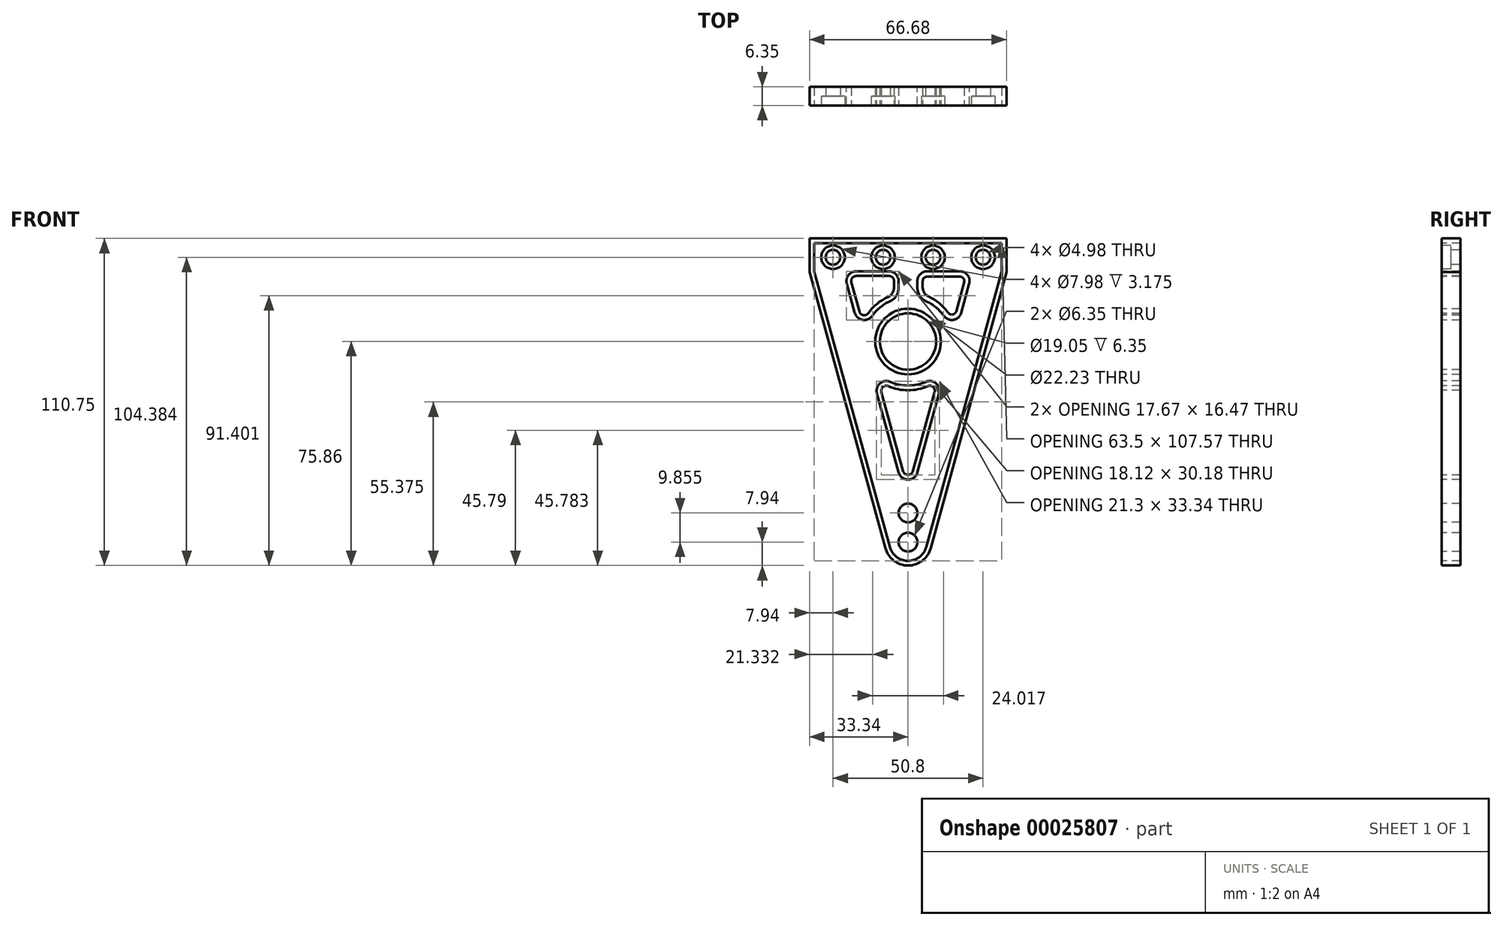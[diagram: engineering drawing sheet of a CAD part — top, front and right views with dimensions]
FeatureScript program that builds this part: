
annotation { "Feature Type Name" : "Feature", "Feature Type Description" : "" }
export const myFeature = defineFeature(function(context is Context, id is Id, definition is map)
    precondition{}
    {
        {
            var Q0;
            Q0=qCreatedBy(makeId("Front.planeOp"),FACE);
            var sketch = newSketch(context, id + "F0", { "sketchPlane" : qUnion([Q0])});
            skCircle(sketch, "E0", {"center": v(0, 0) * mm, "radius": 11.11 * mm});
            skLineSegment(sketch, "E1", {"start": v(0, 0) * mm, "end": v(0, 38.71) * mm, "construction": true});
            skLineSegment(sketch, "E2", {"start": v(0, 0) * mm, "end": v(56.24, 0) * mm, "construction": true});
            skLineSegment(sketch, "E3", {"start": v(0, 33.3) * mm, "end": v(31.75, 33.3) * mm});
            skLineSegment(sketch, "E4", {"start": v(31.75, 33.3) * mm, "end": v(31.75, 23.77) * mm});
            skLineSegment(sketch, "E5", {"start": v(31.75, 23.77) * mm, "end": v(6.12, -69.6) * mm});
            skLineSegment(sketch, "E6", {"start": v(-6.12, -69.6) * mm, "end": v(-31.75, 23.77) * mm});
            skLineSegment(sketch, "E7", {"start": v(-31.75, 23.77) * mm, "end": v(-31.75, 33.3) * mm});
            skLineSegment(sketch, "E8", {"start": v(-31.75, 33.3) * mm, "end": v(0, 33.3) * mm});
            skArc(sketch, "E9", {"start": v(-6.12, -69.6) * mm, "mid": v(0, -74.27) * mm, "end": v(6.12, -69.6) * mm});
            skPoint(sketch, "E10", {"position": v(0, -74.27) * mm});
            skLineSegment(sketch, "E11", {"start": v(-49.73, 28.52) * mm, "end": v(49.74, 28.52) * mm, "construction": true});
            skPoint(sketch, "E12", {"position": v(-25.4, 28.52) * mm});
            skPoint(sketch, "E13", {"position": v(-8.46, 28.52) * mm});
            skPoint(sketch, "E14", {"position": v(8.46, 28.52) * mm});
            skPoint(sketch, "E15", {"position": v(25.4, 28.52) * mm});
            skSolve(sketch);
        }
        {
            var Q0;
            Q0=makeQuery(id+"F0.imprint","IMPRINT",FACE,{"disambiguationData":[TD([[makeQuery(id+"F0.imprint","IMPRINT",EDGE,{"derivedFrom":sQuery(id+"F0.wireOp",EDGE,"E0")}),-1.0]])]});
            extrude(context, id + "F1", {"entities" : qUnion([Q0]), "depth" : 6.35 * mm});
        }
        {
            var Q0;
            Q0=makeQuery(id+"F1.opExtrude","CAP_FACE",FACE,{"disambiguationData":[OSD([sQuery(id+"F0.wireOp",EDGE,"E0"),sQuery(id+"F0.wireOp",EDGE,"E3"),sQuery(id+"F0.wireOp",EDGE,"E4"),sQuery(id+"F0.wireOp",EDGE,"E5"),sQuery(id+"F0.wireOp",EDGE,"E6"),sQuery(id+"F0.wireOp",EDGE,"E7"),sQuery(id+"F0.wireOp",EDGE,"E8"),sQuery(id+"F0.wireOp",EDGE,"E9")])],"isStart":false});
            var sketch = newSketch(context, id + "F2", { "sketchPlane" : qUnion([Q0])});
            skLineSegment(sketch, "E16.0", {"start": v(21.87, 23.77) * mm, "end": v(3.18, 23.77) * mm});
            skLineSegment(sketch, "E16.2", {"start": v(0, -55.92) * mm, "end": v(13.77, -5.75) * mm});
            skLineSegment(sketch, "E16.3", {"start": v(-21.87, 23.77) * mm, "end": v(-14.78, -2.08) * mm});
            skArc(sketch, "E17", {"start": v(14.78, -2.08) * mm, "mid": v(12.25, 8.53) * mm, "end": v(3.18, 14.58) * mm});
            skArc(sketch, "E18.trimOffspring", {"start": v(-13.77, -5.75) * mm, "mid": v(0, -14.92) * mm, "end": v(13.77, -5.75) * mm});
            skLineSegment(sketch, "E19.trimOffspring", {"start": v(-13.77, -5.75) * mm, "end": v(0, -55.92) * mm});
            skLineSegment(sketch, "E20.trimOffspring", {"start": v(14.78, -2.08) * mm, "end": v(21.87, 23.77) * mm});
            skLineSegment(sketch, "E21", {"start": v(0, 0) * mm, "end": v(0, 60.06) * mm, "construction": true});
            skLineSegment(sketch, "E22", {"start": v(-3.18, 14.58) * mm, "end": v(-3.18, 23.77) * mm});
            skLineSegment(sketch, "E23", {"start": v(3.18, 14.58) * mm, "end": v(3.18, 23.77) * mm});
            skLineSegment(sketch, "E24.trimOffspring", {"start": v(-3.17, 23.77) * mm, "end": v(-21.87, 23.77) * mm});
            skArc(sketch, "E25.trimOffspring", {"start": v(-3.18, 14.58) * mm, "mid": v(-12.25, 8.53) * mm, "end": v(-14.78, -2.08) * mm});
            skSolve(sketch);
        }
        {
            var Q0;
            Q0=makeQuery(id+"F2.imprint","IMPRINT",FACE,{"disambiguationData":[TD([[makeQuery(id+"F2.imprint","IMPRINT",EDGE,{"derivedFrom":sQuery(id+"F2.wireOp",EDGE,"E16.3")}),1.0]])]});
            var Q1;
            Q1=makeQuery(id+"F2.imprint","IMPRINT",FACE,{"disambiguationData":[TD([[makeQuery(id+"F2.imprint","IMPRINT",EDGE,{"derivedFrom":sQuery(id+"F2.wireOp",EDGE,"E16.0")}),1.0]])]});
            var Q2;
            Q2=makeQuery(id+"F2.imprint","IMPRINT",FACE,{"disambiguationData":[TD([[makeQuery(id+"F2.imprint","IMPRINT",EDGE,{"derivedFrom":sQuery(id+"F2.wireOp",EDGE,"E16.2")}),1.0]])]});
            extrude(context, id + "F3", {"entities" : qUnion([Q0, Q1, Q2]), "operationType" : NewBodyOperationType.REMOVE, "oppositeDirection" : true, "depth" : 25.4 * mm});
        }
        {
            var Q0;
            Q0=makeQuery(id+"F3.boolean.opBoolean","COPY",EDGE,{"derivedFrom":makeQuery(id+"F3.opExtrude","SWEPT_EDGE",EDGE,{"disambiguationData":[OSD([sQuery(id+"F2.wireOp",EDGE,"E16.3"),sQuery(id+"F2.wireOp",EDGE,"E24.trimOffspring")])]})});
            var Q1;
            Q1=makeQuery(id+"F3.boolean.opBoolean","COPY",EDGE,{"derivedFrom":makeQuery(id+"F3.opExtrude","SWEPT_EDGE",EDGE,{"disambiguationData":[OSD([sQuery(id+"F2.wireOp",EDGE,"E22"),sQuery(id+"F2.wireOp",EDGE,"E24.trimOffspring")])]})});
            var Q2;
            Q2=makeQuery(id+"F3.boolean.opBoolean","COPY",EDGE,{"derivedFrom":makeQuery(id+"F3.opExtrude","SWEPT_EDGE",EDGE,{"disambiguationData":[OSD([sQuery(id+"F2.wireOp",EDGE,"E16.0"),sQuery(id+"F2.wireOp",EDGE,"E20.trimOffspring")])]})});
            var Q3;
            Q3=makeQuery(id+"F3.boolean.opBoolean","COPY",EDGE,{"derivedFrom":makeQuery(id+"F3.opExtrude","SWEPT_EDGE",EDGE,{"disambiguationData":[OSD([sQuery(id+"F2.wireOp",EDGE,"E16.0"),sQuery(id+"F2.wireOp",EDGE,"E23")])]})});
            var Q4;
            Q4=makeQuery(id+"F3.boolean.opBoolean","COPY",EDGE,{"derivedFrom":makeQuery(id+"F3.opExtrude","SWEPT_EDGE",EDGE,{"disambiguationData":[OSD([sQuery(id+"F2.wireOp",EDGE,"E16.2"),sQuery(id+"F2.wireOp",EDGE,"E19.trimOffspring")])]})});
            fillet(context, id + "F4", {"entities" : qUnion([Q0, Q1, Q2, Q3, Q4]), "radius" : 3.3 * mm, "tangentPropagation" : true, "allowEdgeOverflow" : false});
        }
        {
            var Q0;
            Q0=makeQuery(id+"F3.boolean.opBoolean","COPY",EDGE,{"derivedFrom":makeQuery(id+"F3.opExtrude","SWEPT_EDGE",EDGE,{"disambiguationData":[OSD([sQuery(id+"F2.wireOp",EDGE,"E22"),sQuery(id+"F2.wireOp",EDGE,"E25.trimOffspring")])]})});
            var Q1;
            Q1=makeQuery(id+"F3.boolean.opBoolean","COPY",EDGE,{"derivedFrom":makeQuery(id+"F3.opExtrude","SWEPT_EDGE",EDGE,{"disambiguationData":[OSD([sQuery(id+"F2.wireOp",EDGE,"E17"),sQuery(id+"F2.wireOp",EDGE,"E23")])]})});
            fillet(context, id + "F5", {"entities" : qUnion([Q0, Q1]), "radius" : 5.08 * mm, "tangentPropagation" : true, "allowEdgeOverflow" : false});
        }
        {
            var Q0;
            Q0=makeQuery(id+"F3.boolean.opBoolean","COPY",EDGE,{"derivedFrom":makeQuery(id+"F3.opExtrude","SWEPT_EDGE",EDGE,{"disambiguationData":[OSD([sQuery(id+"F2.wireOp",EDGE,"E16.3"),sQuery(id+"F2.wireOp",EDGE,"E25.trimOffspring")])]})});
            var Q1;
            Q1=makeQuery(id+"F3.boolean.opBoolean","COPY",EDGE,{"derivedFrom":makeQuery(id+"F3.opExtrude","SWEPT_EDGE",EDGE,{"disambiguationData":[OSD([sQuery(id+"F2.wireOp",EDGE,"E16.2"),sQuery(id+"F2.wireOp",EDGE,"E18.trimOffspring")])]})});
            var Q2;
            Q2=makeQuery(id+"F3.boolean.opBoolean","COPY",EDGE,{"derivedFrom":makeQuery(id+"F3.opExtrude","SWEPT_EDGE",EDGE,{"disambiguationData":[OSD([sQuery(id+"F2.wireOp",EDGE,"E18.trimOffspring"),sQuery(id+"F2.wireOp",EDGE,"E19.trimOffspring")])]})});
            var Q3;
            Q3=makeQuery(id+"F3.boolean.opBoolean","COPY",EDGE,{"derivedFrom":makeQuery(id+"F3.opExtrude","SWEPT_EDGE",EDGE,{"disambiguationData":[OSD([sQuery(id+"F2.wireOp",EDGE,"E17"),sQuery(id+"F2.wireOp",EDGE,"E20.trimOffspring")])]})});
            fillet(context, id + "F6", {"entities" : qUnion([Q0, Q1, Q2, Q3]), "radius" : 3.3 * mm, "tangentPropagation" : true, "allowEdgeOverflow" : false});
        }
        {
            var Q0;
            Q0=makeQuery(id+"F1.opExtrude","CAP_FACE",FACE,{"disambiguationData":[OSD([sQuery(id+"F0.wireOp",EDGE,"E0"),sQuery(id+"F0.wireOp",EDGE,"E3"),sQuery(id+"F0.wireOp",EDGE,"E4"),sQuery(id+"F0.wireOp",EDGE,"E5"),sQuery(id+"F0.wireOp",EDGE,"E6"),sQuery(id+"F0.wireOp",EDGE,"E7"),sQuery(id+"F0.wireOp",EDGE,"E8"),sQuery(id+"F0.wireOp",EDGE,"E9")])],"isStart":false});
            var sketch = newSketch(context, id + "F7", { "sketchPlane" : qUnion([Q0])});
            skLineSegment(sketch, "E26", {"start": v(-39.8, 28.52) * mm, "end": v(45.62, 28.52) * mm});
            skPoint(sketch, "E27", {"position": v(-25.4, 28.52) * mm});
            skPoint(sketch, "E28", {"position": v(-8.46, 28.52) * mm});
            skPoint(sketch, "E29", {"position": v(8.46, 28.52) * mm});
            skPoint(sketch, "E30", {"position": v(25.4, 28.52) * mm});
            skLineSegment(sketch, "E31", {"start": v(0, 28.52) * mm, "end": v(0, -114.68) * mm});
            skSolve(sketch);
        }
        {
            var Q0;
            Q0=sQuery(id+"F7.wireOp",VERTEX,"E27");
            var Q1;
            Q1=sQuery(id+"F7.wireOp",VERTEX,"E28");
            var Q2;
            Q2=sQuery(id+"F7.wireOp",VERTEX,"E29");
            var Q3;
            Q3=sQuery(id+"F7.wireOp",VERTEX,"E30");
            var Q4;
            Q4=makeQuery(id+"F1.opExtrude","SWEPT_BODY",BODY,{"disambiguationData":[OSD([sQuery(id+"F0.wireOp",EDGE,"E0"),sQuery(id+"F0.wireOp",EDGE,"E3"),sQuery(id+"F0.wireOp",EDGE,"E4"),sQuery(id+"F0.wireOp",EDGE,"E5"),sQuery(id+"F0.wireOp",EDGE,"E6"),sQuery(id+"F0.wireOp",EDGE,"E7"),sQuery(id+"F0.wireOp",EDGE,"E8"),sQuery(id+"F0.wireOp",EDGE,"E9")])]});
            hole(context, id + "F8", {"style" : HoleStyle.C_BORE, "holeDiameter" : 4.98 * mm, "cBoreDiameter" : 7.98 * mm, "cBoreDepth" : 3.17 * mm, "endStyle" : HoleEndStyle.THROUGH, "locations" : qUnion([Q0, Q1, Q2, Q3]), "scope" : qUnion([Q4])});
        }
        {
            var Q0;
            Q0=makeQuery(id+"F1.opExtrude","CAP_FACE",FACE,{"disambiguationData":[OSD([sQuery(id+"F0.wireOp",EDGE,"E0"),sQuery(id+"F0.wireOp",EDGE,"E3"),sQuery(id+"F0.wireOp",EDGE,"E4"),sQuery(id+"F0.wireOp",EDGE,"E5"),sQuery(id+"F0.wireOp",EDGE,"E6"),sQuery(id+"F0.wireOp",EDGE,"E7"),sQuery(id+"F0.wireOp",EDGE,"E8"),sQuery(id+"F0.wireOp",EDGE,"E9")])],"isStart":false});
            var sketch = newSketch(context, id + "F9", { "sketchPlane" : qUnion([Q0])});
            skLineSegment(sketch, "E32", {"start": v(0, 44.3) * mm, "end": v(0, -86.28) * mm});
            skPoint(sketch, "E33", {"position": v(0, -58.06) * mm});
            skPoint(sketch, "E34", {"position": v(0, -67.92) * mm});
            skSolve(sketch);
        }
        {
            var Q0;
            Q0=sQuery(id+"F9.wireOp",VERTEX,"E33");
            var Q1;
            Q1=sQuery(id+"F9.wireOp",VERTEX,"E34");
            var Q2;
            Q2=makeQuery(id+"F1.opExtrude","SWEPT_BODY",BODY,{"disambiguationData":[OSD([sQuery(id+"F0.wireOp",EDGE,"E0"),sQuery(id+"F0.wireOp",EDGE,"E3"),sQuery(id+"F0.wireOp",EDGE,"E4"),sQuery(id+"F0.wireOp",EDGE,"E5"),sQuery(id+"F0.wireOp",EDGE,"E6"),sQuery(id+"F0.wireOp",EDGE,"E7"),sQuery(id+"F0.wireOp",EDGE,"E8"),sQuery(id+"F0.wireOp",EDGE,"E9")])]});
            hole(context, id + "F10", {"style" : HoleStyle.SIMPLE, "holeDiameter" : 6.35 * mm, "endStyle" : HoleEndStyle.THROUGH, "locations" : qUnion([Q0, Q1]), "scope" : qUnion([Q2])});
        }
        {
            var Q0;
            Q0=makeQuery(id+"F1.opExtrude","CAP_FACE",FACE,{"disambiguationData":[OSD([sQuery(id+"F0.wireOp",EDGE,"E0"),sQuery(id+"F0.wireOp",EDGE,"E3"),sQuery(id+"F0.wireOp",EDGE,"E4"),sQuery(id+"F0.wireOp",EDGE,"E5"),sQuery(id+"F0.wireOp",EDGE,"E6"),sQuery(id+"F0.wireOp",EDGE,"E7"),sQuery(id+"F0.wireOp",EDGE,"E8"),sQuery(id+"F0.wireOp",EDGE,"E9")])],"isStart":false});
            var sketch = newSketch(context, id + "F11", { "sketchPlane" : qUnion([Q0])});
            skLineSegment(sketch, "E35.0", {"start": v(-7.65, -70.02) * mm, "end": v(-33.34, 23.56) * mm});
            skArc(sketch, "E35.1", {"start": v(-7.65, -70.02) * mm, "mid": v(0, -75.86) * mm, "end": v(7.65, -70.02) * mm});
            skLineSegment(sketch, "E35.2", {"start": v(33.34, 23.56) * mm, "end": v(7.65, -70.02) * mm});
            skLineSegment(sketch, "E35.3", {"start": v(33.34, 34.89) * mm, "end": v(33.34, 23.56) * mm});
            skLineSegment(sketch, "E35.4", {"start": v(-33.34, 34.89) * mm, "end": v(33.34, 34.89) * mm});
            skLineSegment(sketch, "E35.5", {"start": v(-33.34, 23.56) * mm, "end": v(-33.34, 34.89) * mm});
            skCircle(sketch, "E36.0", {"center": v(0, 0) * mm, "radius": 9.53 * mm});
            skArc(sketch, "E37.0", {"start": v(-4.76, 18.22) * mm, "mid": v(-5.32, 16.33) * mm, "end": v(-6.81, 15.04) * mm});
            skLineSegment(sketch, "E37.1", {"start": v(-4.76, 18.22) * mm, "end": v(-4.76, 20.47) * mm});
            skArc(sketch, "E37.2", {"start": v(-6.48, 22.19) * mm, "mid": v(-5.26, 21.68) * mm, "end": v(-4.76, 20.47) * mm});
            skLineSegment(sketch, "E37.3", {"start": v(-6.48, 22.19) * mm, "end": v(-17.54, 22.19) * mm});
            skArc(sketch, "E37.4", {"start": v(-19.2, 20.02) * mm, "mid": v(-18.9, 21.51) * mm, "end": v(-17.54, 22.19) * mm});
            skArc(sketch, "E37.5", {"start": v(-6.81, 15.04) * mm, "mid": v(-10.48, 12.75) * mm, "end": v(-13.44, 9.6) * mm});
            skLineSegment(sketch, "E37.6", {"start": v(-19.2, 20.02) * mm, "end": v(-16.48, 10.14) * mm});
            skArc(sketch, "E37.7", {"start": v(-13.44, 9.6) * mm, "mid": v(-15.13, 8.9) * mm, "end": v(-16.48, 10.14) * mm});
            skArc(sketch, "E38.0", {"start": v(16.28, 10.2) * mm, "mid": v(15.1, 9.11) * mm, "end": v(13.6, 9.72) * mm});
            skLineSegment(sketch, "E38.1", {"start": v(16.28, 10.2) * mm, "end": v(19, 20.07) * mm});
            skArc(sketch, "E38.2", {"start": v(17.54, 21.98) * mm, "mid": v(18.74, 21.38) * mm, "end": v(19, 20.07) * mm});
            skLineSegment(sketch, "E38.3", {"start": v(17.54, 21.98) * mm, "end": v(6.48, 21.98) * mm});
            skArc(sketch, "E38.4", {"start": v(4.97, 20.47) * mm, "mid": v(5.41, 21.54) * mm, "end": v(6.48, 21.98) * mm});
            skArc(sketch, "E38.5", {"start": v(13.6, 9.72) * mm, "mid": v(10.62, 12.92) * mm, "end": v(6.9, 15.23) * mm});
            skLineSegment(sketch, "E38.6", {"start": v(4.97, 18.22) * mm, "end": v(4.97, 20.47) * mm});
            skArc(sketch, "E38.7", {"start": v(6.9, 15.23) * mm, "mid": v(5.5, 16.44) * mm, "end": v(4.97, 18.22) * mm});
            skArc(sketch, "E39.0", {"start": v(-6.66, -15.1) * mm, "mid": v(0, -16.51) * mm, "end": v(6.66, -15.1) * mm});
            skArc(sketch, "E39.1", {"start": v(-9, -17.13) * mm, "mid": v(-8.47, -15.38) * mm, "end": v(-6.66, -15.1) * mm});
            skLineSegment(sketch, "E39.2", {"start": v(-9, -17.13) * mm, "end": v(-1.65, -43.9) * mm});
            skArc(sketch, "E39.3", {"start": v(1.65, -43.9) * mm, "mid": v(0, -45.16) * mm, "end": v(-1.65, -43.9) * mm});
            skLineSegment(sketch, "E39.4", {"start": v(1.65, -43.9) * mm, "end": v(9, -17.13) * mm});
            skArc(sketch, "E39.5", {"start": v(6.66, -15.1) * mm, "mid": v(8.47, -15.38) * mm, "end": v(9, -17.13) * mm});
            skLineSegment(sketch, "E40.0", {"start": v(31.75, 23.77) * mm, "end": v(6.12, -69.6) * mm});
            skArc(sketch, "E41.0", {"start": v(-6.12, -69.6) * mm, "mid": v(0, -74.27) * mm, "end": v(6.12, -69.6) * mm});
            skLineSegment(sketch, "E42.0", {"start": v(-6.12, -69.6) * mm, "end": v(-31.75, 23.77) * mm});
            skLineSegment(sketch, "E43.0", {"start": v(-10.53, -17.55) * mm, "end": v(-3.18, -44.32) * mm});
            skArc(sketch, "E44.0", {"start": v(3.18, -44.32) * mm, "mid": v(0, -46.75) * mm, "end": v(-3.18, -44.32) * mm});
            skLineSegment(sketch, "E45.0", {"start": v(3.18, -44.32) * mm, "end": v(10.53, -17.55) * mm});
            skArc(sketch, "E46.0", {"start": v(6.02, -13.66) * mm, "mid": v(9.5, -14.18) * mm, "end": v(10.53, -17.55) * mm});
            skArc(sketch, "E47.0", {"start": v(-6.02, -13.66) * mm, "mid": v(0, -14.92) * mm, "end": v(6.02, -13.66) * mm});
            skArc(sketch, "E48.0", {"start": v(-10.53, -17.55) * mm, "mid": v(-9.5, -14.18) * mm, "end": v(-6.02, -13.66) * mm});
            skCircle(sketch, "E49.0", {"center": v(0, 0) * mm, "radius": 11.11 * mm});
            skLineSegment(sketch, "E50.0", {"start": v(31.75, 33.3) * mm, "end": v(31.75, 23.77) * mm});
            skLineSegment(sketch, "E51.0", {"start": v(-31.75, 33.3) * mm, "end": v(31.75, 33.3) * mm});
            skLineSegment(sketch, "E52.0", {"start": v(-31.75, 23.77) * mm, "end": v(-31.75, 33.3) * mm});
            skArc(sketch, "E53.0", {"start": v(-12.14, 8.67) * mm, "mid": v(-15.4, 7.34) * mm, "end": v(-18.01, 9.72) * mm});
            skLineSegment(sketch, "E54.0", {"start": v(-20.73, 19.6) * mm, "end": v(-18.01, 9.72) * mm});
            skArc(sketch, "E55.0", {"start": v(-20.73, 19.6) * mm, "mid": v(-20.17, 22.47) * mm, "end": v(-17.54, 23.77) * mm});
            skLineSegment(sketch, "E56.0", {"start": v(-6.48, 23.77) * mm, "end": v(-17.54, 23.77) * mm});
            skArc(sketch, "E57.0", {"start": v(-6.48, 23.77) * mm, "mid": v(-4.14, 22.8) * mm, "end": v(-3.17, 20.47) * mm});
            skLineSegment(sketch, "E58.0", {"start": v(-3.18, 18.22) * mm, "end": v(-3.18, 20.47) * mm});
            skArc(sketch, "E59.0", {"start": v(-3.17, 18.22) * mm, "mid": v(-3.99, 15.47) * mm, "end": v(-6.16, 13.6) * mm});
            skArc(sketch, "E60.0", {"start": v(-6.16, 13.6) * mm, "mid": v(-9.48, 11.53) * mm, "end": v(-12.14, 8.67) * mm});
            skArc(sketch, "E61.0", {"start": v(18.01, 9.72) * mm, "mid": v(15.4, 7.34) * mm, "end": v(12.14, 8.67) * mm});
            skArc(sketch, "E62.0", {"start": v(12.14, 8.67) * mm, "mid": v(9.48, 11.53) * mm, "end": v(6.16, 13.6) * mm});
            skArc(sketch, "E63.0", {"start": v(6.16, 13.6) * mm, "mid": v(3.99, 15.47) * mm, "end": v(3.17, 18.22) * mm});
            skArc(sketch, "E64.0", {"start": v(3.17, 20.47) * mm, "mid": v(4.14, 22.8) * mm, "end": v(6.48, 23.77) * mm});
            skLineSegment(sketch, "E65.0", {"start": v(3.18, 18.22) * mm, "end": v(3.18, 20.47) * mm});
            skLineSegment(sketch, "E66.0", {"start": v(17.54, 23.77) * mm, "end": v(6.48, 23.77) * mm});
            skArc(sketch, "E67.0", {"start": v(17.54, 23.77) * mm, "mid": v(20.17, 22.47) * mm, "end": v(20.73, 19.6) * mm});
            skLineSegment(sketch, "E68.0", {"start": v(18.01, 9.72) * mm, "end": v(20.73, 19.6) * mm});
            skSolve(sketch);
        }
        {
            var Q0;
            Q0 = qSketchRegion(id + "F11", true);
            var Q1;
            Q1=makeQuery(id+"F11.imprint","IMPRINT",FACE,{"disambiguationData":[TD([[makeQuery(id+"F11.imprint","IMPRINT",EDGE,{"derivedFrom":sQuery(id+"F11.wireOp",EDGE,"E39.0")}),1.0]])]});
            var Q2;
            Q2=makeQuery(id+"F11.imprint","IMPRINT",FACE,{"disambiguationData":[TD([[makeQuery(id+"F11.imprint","IMPRINT",EDGE,{"derivedFrom":sQuery(id+"F11.wireOp",EDGE,"E36.0")}),-1.0]])]});
            var Q3;
            Q3=makeQuery(id+"F11.imprint","IMPRINT",FACE,{"disambiguationData":[TD([[makeQuery(id+"F11.imprint","IMPRINT",EDGE,{"derivedFrom":sQuery(id+"F11.wireOp",EDGE,"E38.0")}),1.0]])]});
            var Q4;
            Q4=makeQuery(id+"F11.imprint","IMPRINT",FACE,{"disambiguationData":[TD([[makeQuery(id+"F11.imprint","IMPRINT",EDGE,{"derivedFrom":sQuery(id+"F11.wireOp",EDGE,"E37.0")}),1.0]])]});
            var Q5;
            Q5=makeQuery(id+"F1.opExtrude","CAP_FACE",FACE,{"disambiguationData":[OSD([sQuery(id+"F0.wireOp",EDGE,"E0"),sQuery(id+"F0.wireOp",EDGE,"E3"),sQuery(id+"F0.wireOp",EDGE,"E4"),sQuery(id+"F0.wireOp",EDGE,"E5"),sQuery(id+"F0.wireOp",EDGE,"E6"),sQuery(id+"F0.wireOp",EDGE,"E7"),sQuery(id+"F0.wireOp",EDGE,"E8"),sQuery(id+"F0.wireOp",EDGE,"E9")])],"isStart":true});
            extrude(context, id + "F12", {"entities" : qUnion([Q0, Q1, Q2, Q3, Q4]), "endBound" : BoundingType.UP_TO_SURFACE, "oppositeDirection" : true, "endBoundEntityFace" : qUnion([Q5]), "depth" : 1.59 * mm});
        }
    });
